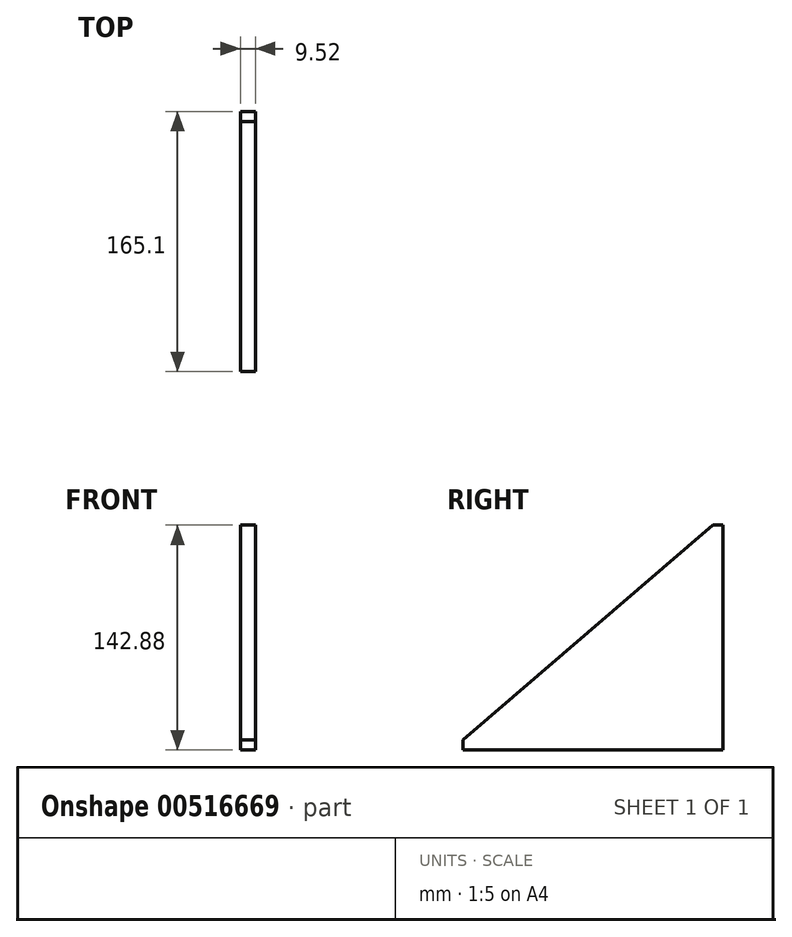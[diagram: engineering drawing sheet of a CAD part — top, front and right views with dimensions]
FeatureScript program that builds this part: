
annotation { "Feature Type Name" : "Feature", "Feature Type Description" : "" }
export const myFeature = defineFeature(function(context is Context, id is Id, definition is map)
    precondition{}
    {
        {
            var Q0;
            Q0=qCreatedBy(makeId("Right.planeOp"),FACE);
            var sketch = newSketch(context, id + "F0", { "sketchPlane" : qUnion([Q0])});
            skLineSegment(sketch, "E0", {"start": v(0, 0) * mm, "end": v(0, 142.88) * mm});
            skLineSegment(sketch, "E1", {"start": v(0, 142.88) * mm, "end": v(-6.35, 142.88) * mm});
            skLineSegment(sketch, "E2", {"start": v(-6.35, 142.88) * mm, "end": v(-165.1, 6.35) * mm});
            skLineSegment(sketch, "E3", {"start": v(-165.1, 6.35) * mm, "end": v(-165.1, 0) * mm});
            skLineSegment(sketch, "E4", {"start": v(-165.1, 0) * mm, "end": v(0, 0) * mm});
            skSolve(sketch);
        }
        {
            var Q0;
            Q0=makeQuery(id+"F0.imprint","IMPRINT",FACE,{"disambiguationData":[TD([[makeQuery(id+"F0.imprint","IMPRINT",EDGE,{"derivedFrom":sQuery(id+"F0.wireOp",EDGE,"E0")}),1.0]])]});
            extrude(context, id + "F1", {"entities" : qUnion([Q0]), "endBound" : BoundingType.SYMMETRIC, "depth" : 9.52 * mm, "offsetDistance" : 25.4 * mm});
        }
    });
